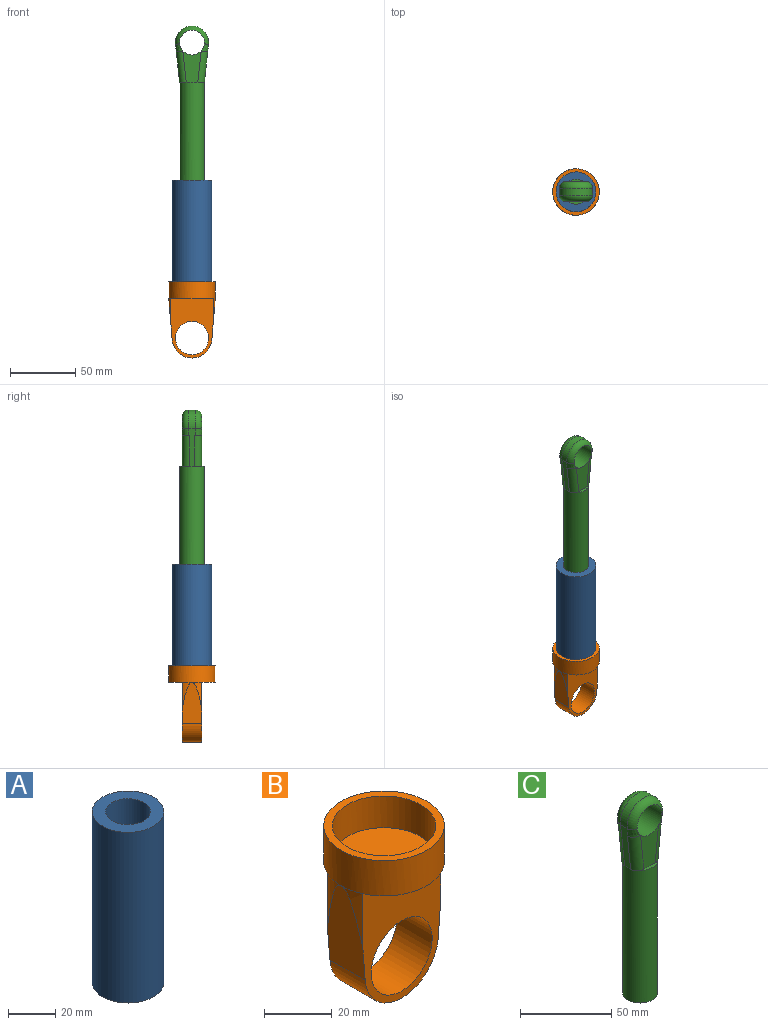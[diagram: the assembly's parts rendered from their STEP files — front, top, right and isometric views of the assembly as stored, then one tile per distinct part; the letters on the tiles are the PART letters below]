
ASSEMBLY  parts=3 mates=2
PART A: 5 faces, bbox 30.5x30.5x88.9 mm
  f0: cylinder r=9.53mm len=76.2mm, axis (0,0,-1), area 4560.4mm2, adj f2,f4
  f1: cylinder r=15.24mm len=88.9mm, axis (0,0,-1), area 8512.7mm2, adj f2,f3
  f2: plane 30.48x30.48mm, normal (0,0,1), area 444.6mm2, adj f0,f1
  f3: plane 30.48x30.48mm, normal (0,0,-1), area 729.7mm2, adj f1
  f4: plane 19.05x19.05mm, normal (0,0,1), area 285mm2, adj f0
PART B: 16 faces, bbox 35.6x35.6x58.4 mm
  f0: plane 32.37x10.42mm, normal (0,0,-1), area 242.3mm2, adj f2,f10
  f1: cylinder r=15.24mm len=30.48mm, axis (0,0,1), area 1094.5mm2, adj f4,f5
  f2: cylinder r=17.78mm len=35.56mm, axis (0,0,1), area 1418.8mm2, adj f0,f3,f4,f6,f7,f12,f13,f14
  f3: plane 32.37x10.41mm, normal (0,0,-1), area 242.3mm2, adj f2,f11
  f4: plane 35.56x35.56mm, normal (0,0,1), area 263.5mm2, adj f1,f2
  f5: plane 30.48x30.48mm, normal (0,0,1), area 729.7mm2, adj f1
  f6: plane 31.72x14.73mm, normal (-1,0,-0.08), area 374.3mm2, adj f2,f8,f10,f11,f13,f15
  f7: plane 31.72x14.73mm, normal (1,0,-0.08), area 374.3mm2, adj f2,f8,f10,f11,f12,f14
  f8: cylinder r=15.24mm len=30.38mm, axis (0,-1,0), area 668.7mm2, adj f6,f7,f10,f11
  f9: cylinder r=12.7mm len=25.4mm, axis (0,-1,0), area 1175.6mm2, adj f10,f11
  f10: plane 45.72x32.37mm, normal (0,1,0), area 834.9mm2, adj f0,f6,f7,f8,f9,f14,f15
  f11: plane 45.72x32.37mm, normal (0,-1,0), area 834.9mm2, adj f3,f6,f7,f8,f9,f12,f13
  f12: extruded ~19.56x7.33mm, area 49.8mm2, adj f2,f7,f11
  f13: extruded ~19.56x7.33mm, area 49.8mm2, adj f2,f6,f11
  f14: extruded ~19.56x7.33mm, area 49.8mm2, adj f2,f7,f10
  f15: extruded ~19.56x7.33mm, area 49.8mm2, adj f2,f6,f10
PART C: 24 faces, bbox 27.6x19.2x133.3 mm
  f0: plane 13.16x2.64mm, normal (0,0,1), area 18.2mm2, adj f1,f13,f14,f18
  f1: cylinder r=9.53mm len=88.9mm, axis (0,0,-1), area 5320.4mm2, adj f0,f2,f3,f4,f5,f6,f7
  f2: plane 13.16x2.64mm, normal (0,0,1), area 18.2mm2, adj f1,f12,f19,f23
  f3: plane 19.05x19.05mm, normal (0,0,-1), area 285mm2, adj f1
  f4: plane 7.03x3.09mm, normal (0,0,-1), area 2.5mm2, adj f1,f10,f14
  f5: plane 7.03x3.09mm, normal (0,0,-1), area 2.5mm2, adj f1,f10,f19
  f6: plane 7.03x3.09mm, normal (0,0,-1), area 2.5mm2, adj f1,f8,f18
  f7: plane 7.03x3.09mm, normal (0,0,-1), area 2.5mm2, adj f1,f8,f23
  f8: plane 29.14x5.31mm, normal (0.99,0,-0.11), area 136.1mm2, adj f6,f7,f9,f17,f18,f22,f23
  f9: cylinder r=12.7mm len=25.4mm, axis (0,1,0), area 226.3mm2, adj f8,f10,f16,f21
  f10: plane 29.14x5.31mm, normal (-0.99,0,-0.11), area 136.1mm2, adj f4,f5,f9,f14,f15,f19,f20
  f11: cylinder r=9.53mm len=19.05mm, axis (0,1,0), area 881.7mm2, adj f12,f13,f15,f16,f17,f20,f21,f22
  f12: plane 23.99x13.94mm, normal (0,-1,0), area 243.9mm2, adj f2,f11,f19,f23
  f13: plane 23.99x13.94mm, normal (0,1,0), area 243.9mm2, adj f0,f11,f14,f18
  f14: cylinder r=5.08mm len=24.53mm, axis (0.11,0,-0.99), area 190mm2, adj f0,f4,f10,f13,f15
  f15: bspline ~8.1x6.24mm, area 38.1mm2, adj f10,f11,f14,f16
  f16: torus R=7.62mm, axis (0,1,0), area 234.3mm2, adj f9,f11,f15,f17
  f17: bspline ~8.44x6.42mm, area 38.1mm2, adj f8,f11,f16,f18
  f18: cylinder r=5.08mm len=24.53mm, axis (0.11,0,0.99), area 190mm2, adj f0,f6,f8,f13,f17
  f19: cylinder r=5.08mm len=24.53mm, axis (-0.11,0,0.99), area 190mm2, adj f2,f5,f10,f12,f20
  f20: bspline ~8.44x6.42mm, area 38.1mm2, adj f10,f11,f19,f21
  f21: torus R=7.62mm, axis (0,-1,0), area 234.3mm2, adj f9,f11,f20,f22
  f22: bspline ~8.1x6.24mm, area 38.1mm2, adj f8,f11,f21,f23
  f23: cylinder r=5.08mm len=24.53mm, axis (-0.11,0,-0.99), area 190mm2, adj f2,f7,f8,f12,f22
PLACE A t=(-1.53,-2.21,-15.03)mm fixed
PLACE B t=(-1.53,-2.21,-3.6)mm
PLACE C t=(-1.53,-2.21,-31.54)mm
MATE fastened A.f1 <-> B.f1  axis (0,0,-1) through (-1.53,-2.21,-15.03)mm
MATE slider C.f1 <-> A.f0  axis (0,0,-1) through (-1.53,-2.21,104.35)mm
